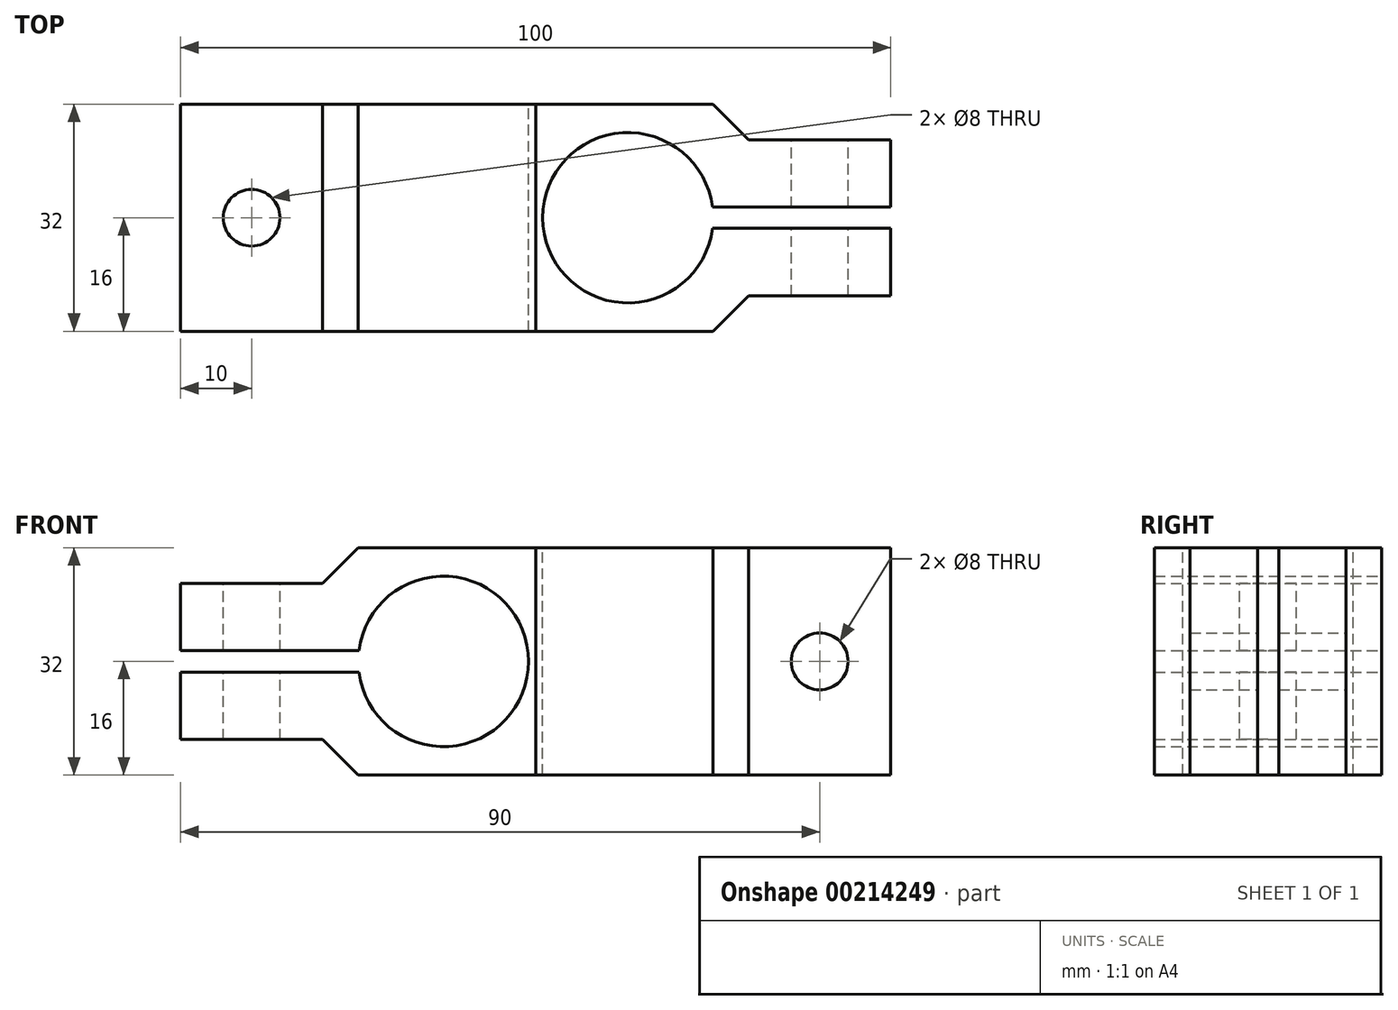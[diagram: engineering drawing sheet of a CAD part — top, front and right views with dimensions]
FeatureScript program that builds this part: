
annotation { "Feature Type Name" : "Feature", "Feature Type Description" : "" }
export const myFeature = defineFeature(function(context is Context, id is Id, definition is map)
    precondition{}
    {
        {
            var Q0;
            Q0=qCreatedBy(makeId("Front.planeOp"),FACE);
            var sketch = newSketch(context, id + "F0", { "sketchPlane" : qUnion([Q0])});
            skArc(sketch, "E0", {"start": v(-1, 0) * mm, "mid": v(-12.25, 11.98) * mm, "end": v(-24.9, 1.5) * mm});
            skLineSegment(sketch, "E1", {"start": v(0, 16) * mm, "end": v(-25, 16) * mm});
            skLineSegment(sketch, "E2", {"start": v(-25, 16) * mm, "end": v(-30, 11) * mm});
            skLineSegment(sketch, "E3", {"start": v(-30, 11) * mm, "end": v(-50, 11) * mm});
            skLineSegment(sketch, "E4", {"start": v(-50, 11) * mm, "end": v(-50, 1.5) * mm});
            skLineSegment(sketch, "E5", {"start": v(-50, 1.5) * mm, "end": v(-24.9, 1.5) * mm});
            skLineSegment(sketch, "E6", {"start": v(-58.54, 0) * mm, "end": v(16.55, 0) * mm, "construction": true});
            skLineSegment(sketch, "E7", {"start": v(0, 16) * mm, "end": v(0, 0) * mm});
            skLineSegment(sketch, "E8.MirrorCS", {"start": v(-25, -16) * mm, "end": v(-30, -11) * mm});
            skLineSegment(sketch, "E9.MirrorCS", {"start": v(0, -16) * mm, "end": v(0, 0) * mm});
            skLineSegment(sketch, "E10.MirrorCS", {"start": v(-50, -1.5) * mm, "end": v(-24.9, -1.5) * mm});
            skLineSegment(sketch, "E11.MirrorCS", {"start": v(-30, -11) * mm, "end": v(-50, -11) * mm});
            skLineSegment(sketch, "E12.MirrorCS", {"start": v(-50, -11) * mm, "end": v(-50, -1.5) * mm});
            skLineSegment(sketch, "E13.MirrorCS", {"start": v(0, -16) * mm, "end": v(-25, -16) * mm});
            skArc(sketch, "E14.MirrorCS", {"start": v(-1, 0) * mm, "mid": v(-12.25, -11.98) * mm, "end": v(-24.9, -1.5) * mm});
            skLineSegment(sketch, "E15", {"start": v(0, 42.24) * mm, "end": v(0, -34.3) * mm, "construction": true});
            skSolve(sketch);
        }
        {
            var Q0;
            Q0 = qSketchRegion(id + "F0", true);
            extrude(context, id + "F1", {"entities" : qUnion([Q0]), "endBound" : BoundingType.SYMMETRIC, "depth" : 32 * mm});
        }
        {
            var Q0;
            Q0=makeQuery(id+"F1.opExtrude","SWEPT_FACE",FACE,{"disambiguationData":[OSD([sQuery(id+"F0.wireOp",EDGE,"E3")])]});
            var sketch = newSketch(context, id + "F2", { "sketchPlane" : qUnion([Q0])});
            skLineSegment(sketch, "E16", {"start": v(-50, 0) * mm, "end": v(-30, 0) * mm, "construction": true});
            skCircle(sketch, "E17", {"center": v(-40, 0) * mm, "radius": 4 * mm});
            skSolve(sketch);
        }
        {
            var Q0;
            Q0 = qSketchRegion(id + "F2", true);
            extrude(context, id + "F3", {"entities" : qUnion([Q0]), "operationType" : NewBodyOperationType.REMOVE, "endBound" : BoundingType.THROUGH_ALL, "oppositeDirection" : true, "depth" : 25 * mm});
        }
        {
            var Q0;
            Q0=makeQuery(id+"F1.opExtrude","SWEPT_FACE",FACE,{"disambiguationData":[OSD([sQuery(id+"F0.wireOp",EDGE,"E7"),sQuery(id+"F0.wireOp",EDGE,"E9.MirrorCS")])]});
            var sketch = newSketch(context, id + "F4", { "sketchPlane" : qUnion([Q0])});
            skLineSegment(sketch, "E18", {"start": v(16, 16) * mm, "end": v(-16, -16) * mm, "construction": true});
            skSolve(sketch);
        }
        {
            var Q0;
            Q0=makeQuery(id+"F1.opExtrude","SWEPT_BODY",BODY,{"disambiguationData":[OSD([sQuery(id+"F0.wireOp",EDGE,"E0"),sQuery(id+"F0.wireOp",EDGE,"E1"),sQuery(id+"F0.wireOp",EDGE,"E2"),sQuery(id+"F0.wireOp",EDGE,"E3"),sQuery(id+"F0.wireOp",EDGE,"E4"),sQuery(id+"F0.wireOp",EDGE,"E5"),sQuery(id+"F0.wireOp",EDGE,"E7"),sQuery(id+"F0.wireOp",EDGE,"E8.MirrorCS"),sQuery(id+"F0.wireOp",EDGE,"E9.MirrorCS"),sQuery(id+"F0.wireOp",EDGE,"E10.MirrorCS"),sQuery(id+"F0.wireOp",EDGE,"E11.MirrorCS"),sQuery(id+"F0.wireOp",EDGE,"E12.MirrorCS"),sQuery(id+"F0.wireOp",EDGE,"E13.MirrorCS"),sQuery(id+"F0.wireOp",EDGE,"E14.MirrorCS")])]});
            var Q1;
            Q1=sQuery(id+"F4.wireOp",EDGE,"E18");
            transform(context, id + "F5", {"entities" : qUnion([Q0]), "transformType" : TransformType.ROTATION, "transformAxis" : qUnion([Q1]), "angle" : 180 * degree, "makeCopy" : true});
        }
    });
